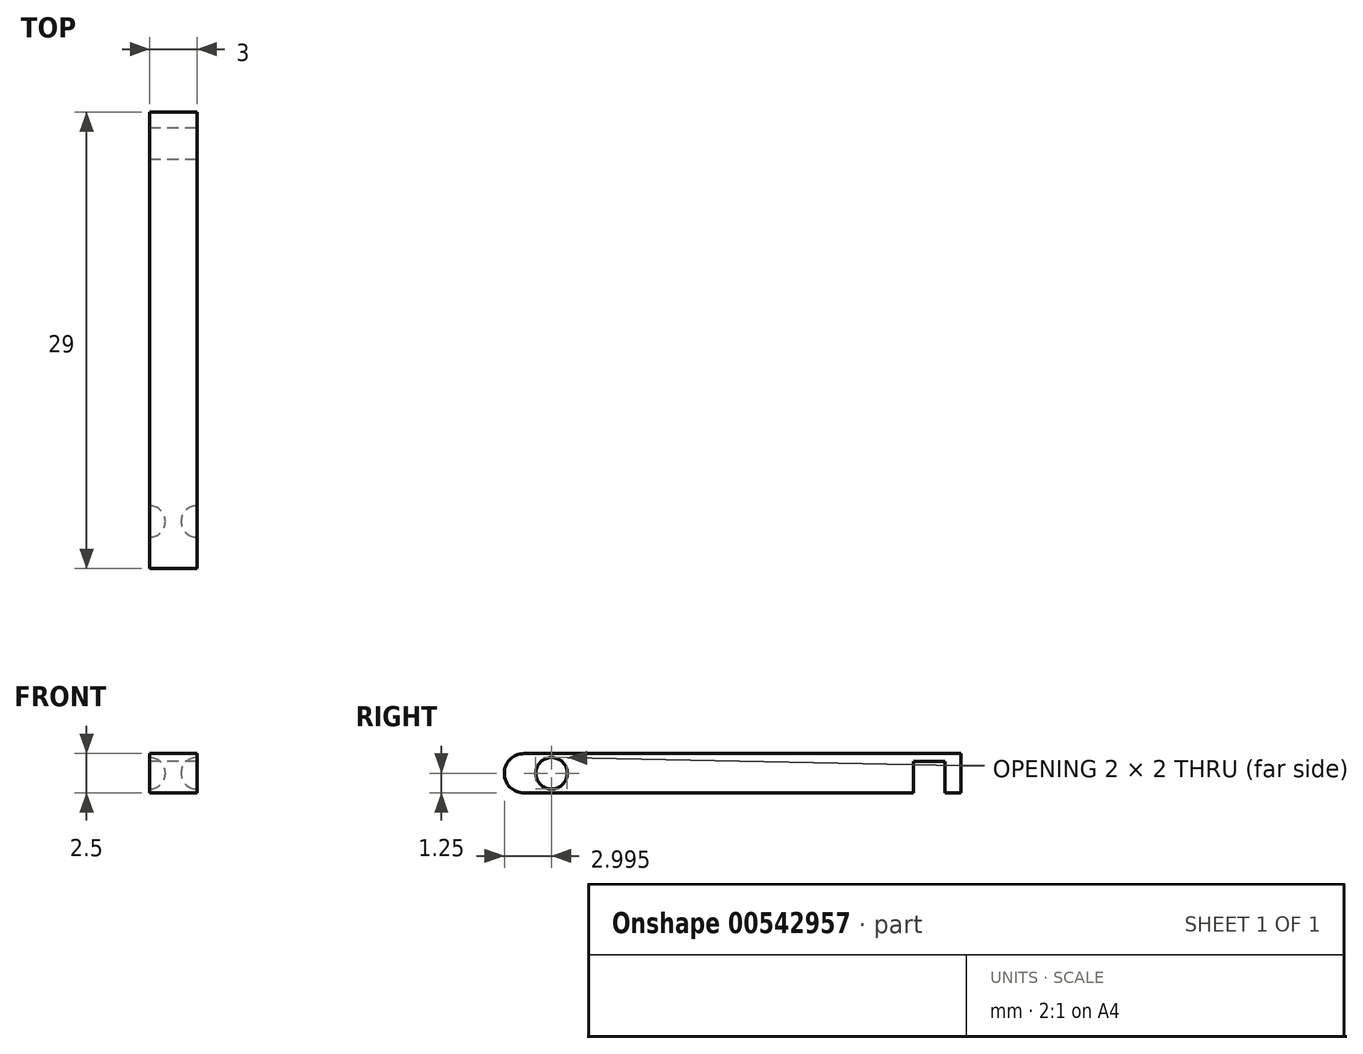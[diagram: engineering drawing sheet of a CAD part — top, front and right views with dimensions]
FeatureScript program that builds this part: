
annotation { "Feature Type Name" : "Feature", "Feature Type Description" : "" }
export const myFeature = defineFeature(function(context is Context, id is Id, definition is map)
    precondition{}
    {
        {
            var Q0;
            Q0=qCreatedBy(makeId("Top.planeOp"),FACE);
            var sketch = newSketch(context, id + "F0", { "sketchPlane" : qUnion([Q0])});
            skLineSegment(sketch, "E0.bottom", {"start": v(-30.11, 22.62) * mm, "end": v(-27.11, 22.62) * mm});
            skLineSegment(sketch, "E0.top", {"start": v(-30.11, -6.38) * mm, "end": v(-27.11, -6.38) * mm});
            skLineSegment(sketch, "E0.left", {"start": v(-30.11, 22.62) * mm, "end": v(-30.11, -6.38) * mm});
            skLineSegment(sketch, "E0.right", {"start": v(-27.11, 22.62) * mm, "end": v(-27.11, -6.38) * mm});
            skSolve(sketch);
        }
        {
            var Q0;
            Q0 = qSketchRegion(id + "F0", true);
            extrude(context, id + "F1", {"entities" : qUnion([Q0]), "depth" : 2.5 * mm, "offsetDistance" : 25 * mm});
        }
        {
            var Q0;
            Q0=makeQuery(id+"F1.opExtrude","SWEPT_FACE",FACE,{"disambiguationData":[OSD([sQuery(id+"F0.wireOp",EDGE,"E0.right")])]});
            var sketch = newSketch(context, id + "F2", { "sketchPlane" : qUnion([Q0])});
            skCircle(sketch, "E1", {"center": v(-3.38, 1.25) * mm, "radius": 1 * mm});
            skPoint(sketch, "E1.centerSnap0", {"position": v(-6.38, 1.25) * mm});
            skLineSegment(sketch, "E2", {"start": v(-3.38, 2.25) * mm, "end": v(-3.38, 0.25) * mm});
            skSolve(sketch);
        }
        {
            var Q0;
            {var subQ0=sQuery(id+"F2.wireOp",EDGE,"E2");Q0=makeQuery(id+"F2.imprint","IMPRINT",FACE,{"disambiguationData":[TD([[makeQuery(id+"F2.imprint","IMPRINT",EDGE,{"derivedFrom":subQ0}),-1.0]])]});}
            var Q1;
            Q1=sQuery(id+"F2.wireOp",EDGE,"E2");
            revolve(context, id + "F3", {"operationType" : NewBodyOperationType.REMOVE, "entities" : qUnion([Q0]), "axis" : qUnion([Q1]), "revolveType" : RevolveType.FULL, "oppositeDirection" : true});
        }
        {
            var Q0;
            Q0=makeQuery(id+"F1.opExtrude","SWEPT_FACE",FACE,{"disambiguationData":[OSD([sQuery(id+"F0.wireOp",EDGE,"E0.left")])]});
            var sketch = newSketch(context, id + "F4", { "sketchPlane" : qUnion([Q0])});
            skCircle(sketch, "E3", {"center": v(3.38, 1.25) * mm, "radius": 1 * mm});
            skPoint(sketch, "E3.centerSnap0", {"position": v(6.38, 1.25) * mm});
            skLineSegment(sketch, "E4", {"start": v(2.38, 1.25) * mm, "end": v(4.38, 1.25) * mm});
            skSolve(sketch);
        }
        {
            var Q0;
            {var subQ0=sQuery(id+"F4.wireOp",EDGE,"E4");Q0=makeQuery(id+"F4.imprint","IMPRINT",FACE,{"disambiguationData":[TD([[makeQuery(id+"F4.imprint","IMPRINT",EDGE,{"derivedFrom":subQ0}),1.0]])]});}
            var Q1;
            Q1=sQuery(id+"F4.wireOp",EDGE,"E4");
            revolve(context, id + "F5", {"operationType" : NewBodyOperationType.REMOVE, "entities" : qUnion([Q0]), "axis" : qUnion([Q1]), "revolveType" : RevolveType.FULL, "oppositeDirection" : true});
        }
        {
            var Q0;
            Q0=makeQuery(id+"F1.opExtrude","CAP_EDGE",EDGE,{"disambiguationData":[OSD([sQuery(id+"F0.wireOp",EDGE,"E0.top")])],"isStart":false});
            var Q1;
            Q1=makeQuery(id+"F1.opExtrude","CAP_EDGE",EDGE,{"disambiguationData":[OSD([sQuery(id+"F0.wireOp",EDGE,"E0.top")])],"isStart":true});
            fillet(context, id + "F6", {"entities" : qUnion([Q0, Q1]), "radius" : 1.25 * mm, "tangentPropagation" : true, "allowEdgeOverflow" : false});
        }
        {
            var Q0;
            Q0=makeQuery(id+"F1.opExtrude","CAP_FACE",FACE,{"disambiguationData":[OSD([sQuery(id+"F0.wireOp",EDGE,"E0.bottom"),sQuery(id+"F0.wireOp",EDGE,"E0.top"),sQuery(id+"F0.wireOp",EDGE,"E0.left"),sQuery(id+"F0.wireOp",EDGE,"E0.right")])],"isStart":true});
            var sketch = newSketch(context, id + "F7", { "sketchPlane" : qUnion([Q0])});
            skLineSegment(sketch, "E5.bottom", {"start": v(-27.11, -21.62) * mm, "end": v(-30.11, -21.62) * mm});
            skLineSegment(sketch, "E5.top", {"start": v(-27.11, -19.62) * mm, "end": v(-30.11, -19.62) * mm});
            skLineSegment(sketch, "E5.left", {"start": v(-27.11, -21.62) * mm, "end": v(-27.11, -19.62) * mm});
            skLineSegment(sketch, "E5.right", {"start": v(-30.11, -21.62) * mm, "end": v(-30.11, -19.62) * mm});
            skSolve(sketch);
        }
        {
            var Q0;
            Q0 = qSketchRegion(id + "F7", true);
            extrude(context, id + "F8", {"entities" : qUnion([Q0]), "operationType" : NewBodyOperationType.REMOVE, "oppositeDirection" : true, "depth" : 2 * mm, "offsetDistance" : 25 * mm});
        }
    });
